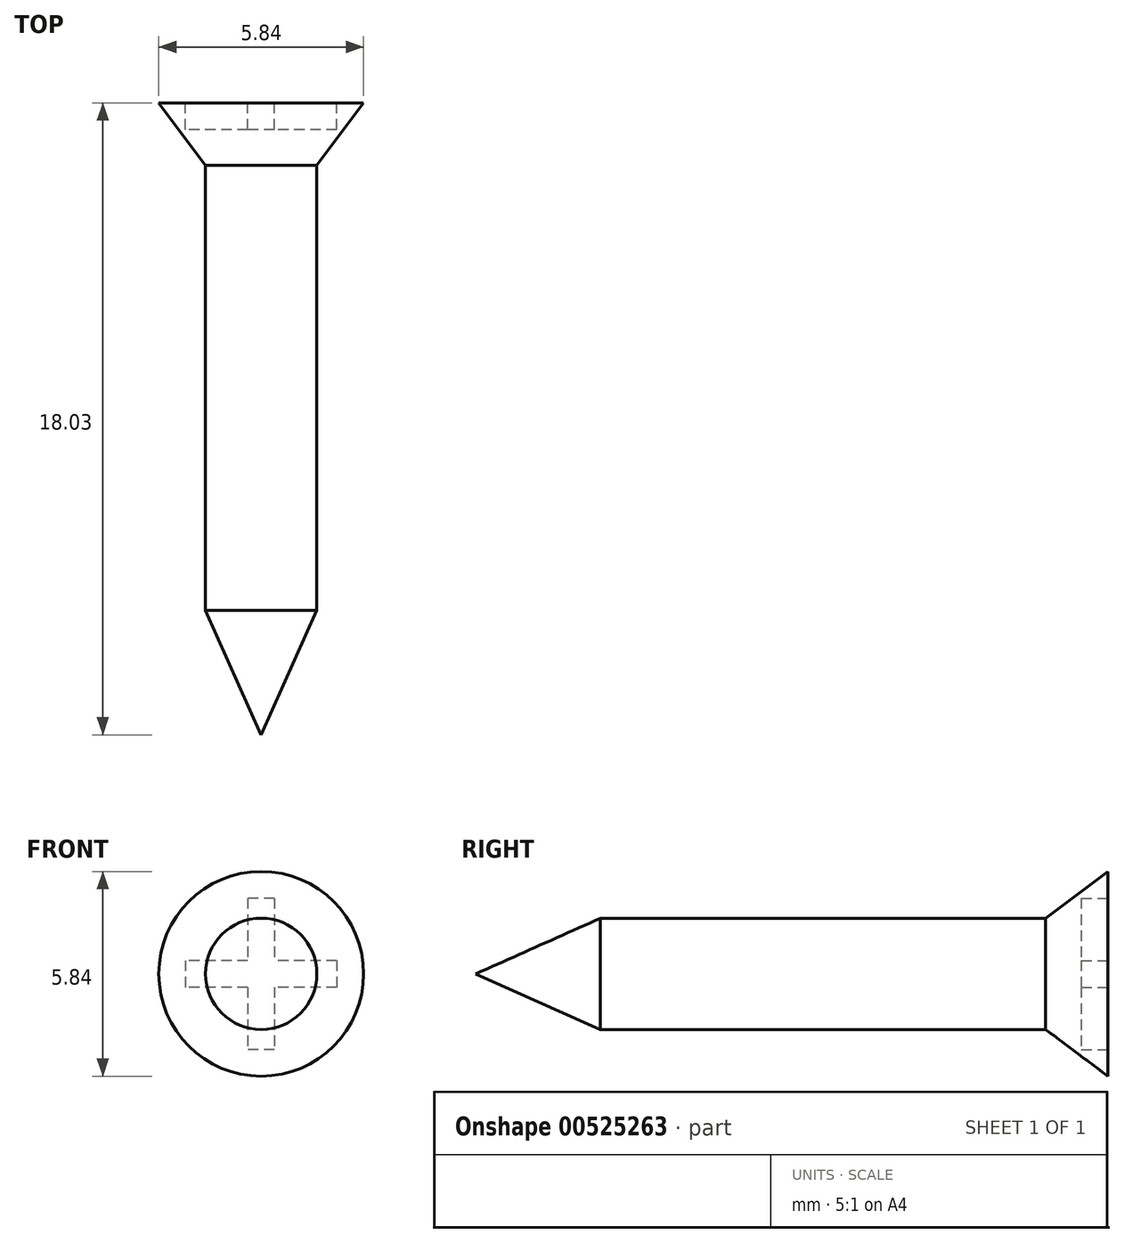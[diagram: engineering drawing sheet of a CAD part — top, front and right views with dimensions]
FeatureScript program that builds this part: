
annotation { "Feature Type Name" : "Feature", "Feature Type Description" : "" }
export const myFeature = defineFeature(function(context is Context, id is Id, definition is map)
    precondition{}
    {
        {
            var Q0;
            Q0=qCreatedBy(makeId("Right.planeOp"),FACE);
            var sketch = newSketch(context, id + "F0", { "sketchPlane" : qUnion([Q0])});
            skLineSegment(sketch, "E0", {"start": v(0, 0) * mm, "end": v(18.03, 0) * mm, "construction": true});
            skLineSegment(sketch, "E1", {"start": v(3.56, 1.59) * mm, "end": v(16.26, 1.59) * mm});
            skLineSegment(sketch, "E2", {"start": v(18.03, 2.92) * mm, "end": v(18.03, 0) * mm});
            skLineSegment(sketch, "E3", {"start": v(3.56, 1.59) * mm, "end": v(0, 0) * mm});
            skLineSegment(sketch, "E4", {"start": v(16.26, 1.59) * mm, "end": v(18.03, 2.92) * mm});
            skPoint(sketch, "E5.orphan", {"position": v(-13.4, 0) * mm});
            skLineSegment(sketch, "E6", {"start": v(0, 0) * mm, "end": v(18.03, 0) * mm});
            skSolve(sketch);
        }
        {
            var Q0;
            Q0 = qSketchRegion(id + "F0", true);
            var Q1;
            Q1=sQuery(id+"F0.wireOp",EDGE,"E6");
            revolve(context, id + "F1", {"entities" : qUnion([Q0]), "axis" : qUnion([Q1]), "revolveType" : RevolveType.FULL});
        }
        {
            var Q0;
            Q0=makeQuery(id+"F1.opRevolve","SWEPT_FACE",FACE,{"disambiguationData":[OSD([sQuery(id+"F0.wireOp",EDGE,"E2")])]});
            var sketch = newSketch(context, id + "F2", { "sketchPlane" : qUnion([Q0])});
            skLineSegment(sketch, "E7", {"start": v(-3.77, 0) * mm, "end": v(4.32, 0) * mm, "construction": true});
            skLineSegment(sketch, "E8", {"start": v(0, 3.23) * mm, "end": v(0, -3.5) * mm, "construction": true});
            skLineSegment(sketch, "E9.0", {"start": v(-0.38, 2.16) * mm, "end": v(-0.38, 0.38) * mm});
            skLineSegment(sketch, "E10.0", {"start": v(0.38, 2.16) * mm, "end": v(0.38, 0.38) * mm});
            skLineSegment(sketch, "E11.0", {"start": v(-2.16, -0.38) * mm, "end": v(-0.38, -0.38) * mm});
            skLineSegment(sketch, "E12.0", {"start": v(-2.16, 0.38) * mm, "end": v(-0.38, 0.38) * mm});
            skLineSegment(sketch, "E13", {"start": v(-0.38, 2.16) * mm, "end": v(0.38, 2.16) * mm});
            skLineSegment(sketch, "E14", {"start": v(-0.38, -2.16) * mm, "end": v(0.38, -2.16) * mm});
            skLineSegment(sketch, "E15", {"start": v(-2.16, 0.38) * mm, "end": v(-2.16, -0.38) * mm});
            skLineSegment(sketch, "E16", {"start": v(2.16, 0.38) * mm, "end": v(2.16, -0.38) * mm});
            skLineSegment(sketch, "E17.trimOffspring", {"start": v(0.38, -0.38) * mm, "end": v(0.38, -2.16) * mm});
            skLineSegment(sketch, "E18.trimOffspring", {"start": v(-0.38, -0.38) * mm, "end": v(-0.38, -2.16) * mm});
            skLineSegment(sketch, "E19.trimOffspring", {"start": v(0.38, -0.38) * mm, "end": v(2.16, -0.38) * mm});
            skLineSegment(sketch, "E20.trimOffspring", {"start": v(0.38, 0.38) * mm, "end": v(2.16, 0.38) * mm});
            skSolve(sketch);
        }
        {
            var Q0;
            Q0=makeQuery(id+"F2.imprint","IMPRINT",FACE,{"disambiguationData":[TD([[makeQuery(id+"F2.imprint","IMPRINT",EDGE,{"derivedFrom":sQuery(id+"F2.wireOp",EDGE,"E9.0")}),1.0]])]});
            extrude(context, id + "F3", {"entities" : qUnion([Q0]), "operationType" : NewBodyOperationType.REMOVE, "oppositeDirection" : true, "depth" : 0.76 * mm, "offsetDistance" : 25.4 * mm});
        }
    });
